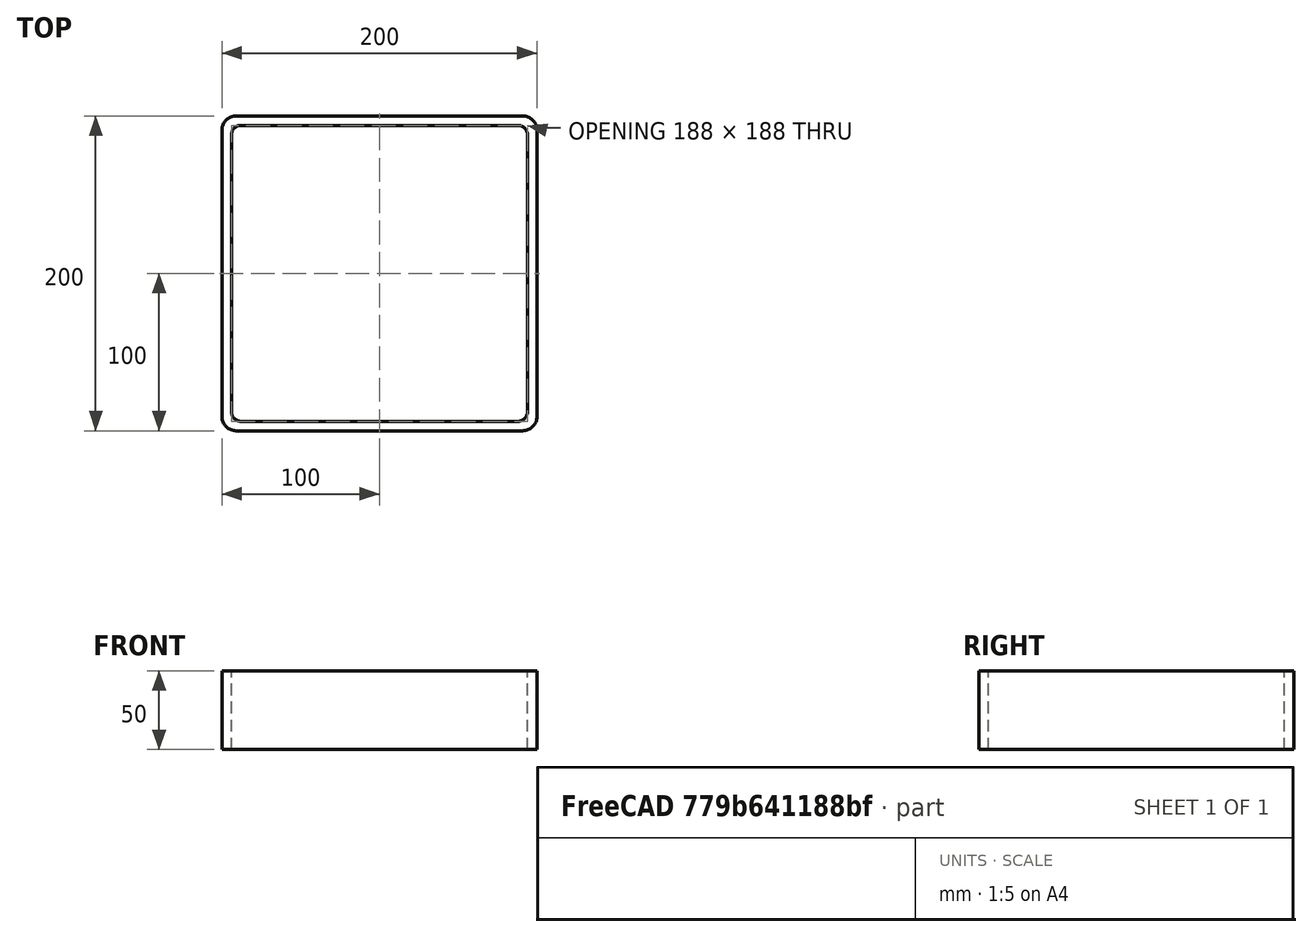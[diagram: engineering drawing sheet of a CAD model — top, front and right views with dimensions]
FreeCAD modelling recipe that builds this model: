
FCSTD DOCUMENT  (FreeCAD 0.15R4671 (Git))
Label: Square hollow section 200x200x6 EN10219 S235JRH
License: All rights reserved
LicenseURL: http://en.wikipedia.org/wiki/All_rights_reserved
objects: Sketcher::SketchObject×1, Part::Extrusion×1
note: 2 computed .brp shape members not serialized (recipe doc carries the construction recipe); baked Part::Feature solids carry a one-line shape summary decoded from their .brp

FEATURE [Sketcher::SketchObject] Sketch
  sketch-geometry (16):
    g0: LineSegment StartX=-88 StartY=94 StartZ=0 EndX=88 EndY=94 EndZ=0
    g1: LineSegment StartX=94 StartY=88 StartZ=0 EndX=94 EndY=-88 EndZ=0
    g2: LineSegment StartX=88 StartY=-94 StartZ=0 EndX=-88 EndY=-94 EndZ=0
    g3: LineSegment StartX=-94 StartY=-88 StartZ=0 EndX=-94 EndY=88 EndZ=0
    g4: LineSegment StartX=-91 StartY=100 StartZ=0 EndX=91 EndY=100 EndZ=0
    g5: LineSegment StartX=100 StartY=91 StartZ=0 EndX=100 EndY=-91 EndZ=0
    g6: LineSegment StartX=91 StartY=-100 StartZ=0 EndX=-91 EndY=-100 EndZ=0
    g7: LineSegment StartX=-100 StartY=-91 StartZ=0 EndX=-100 EndY=91 EndZ=0
    g8: ArcOfCircle CenterX=-88 CenterY=88 CenterZ=0 NormalX=0 NormalY=0 NormalZ=1 Radius=6 StartAngle=1.5708 EndAngle=3.14159
    g9: ArcOfCircle CenterX=88 CenterY=88 CenterZ=0 NormalX=0 NormalY=0 NormalZ=1 Radius=6 StartAngle=0 EndAngle=1.5708
    g10: ArcOfCircle CenterX=88 CenterY=-88 CenterZ=0 NormalX=0 NormalY=0 NormalZ=1 Radius=6 StartAngle=4.71239 EndAngle=6.28319
    g11: ArcOfCircle CenterX=-88 CenterY=-88 CenterZ=0 NormalX=0 NormalY=0 NormalZ=1 Radius=6 StartAngle=3.14159 EndAngle=4.71239
    g12: ArcOfCircle CenterX=91 CenterY=91 CenterZ=0 NormalX=0 NormalY=0 NormalZ=1 Radius=9 StartAngle=0 EndAngle=1.5708
    g13: ArcOfCircle CenterX=91 CenterY=-91 CenterZ=0 NormalX=0 NormalY=0 NormalZ=1 Radius=9 StartAngle=4.71239 EndAngle=6.28319
    g14: ArcOfCircle CenterX=-91 CenterY=-91 CenterZ=0 NormalX=0 NormalY=0 NormalZ=1 Radius=9 StartAngle=3.14159 EndAngle=4.71239
    g15: ArcOfCircle CenterX=-91 CenterY=91 CenterZ=0 NormalX=0 NormalY=0 NormalZ=1 Radius=9 StartAngle=1.5708 EndAngle=3.14159
  constraints (36):
    c: Horizontal(g2)
    c: Vertical(g3)
    c: Horizontal(g6)
    c: Vertical(g7)
    c: Tangent(g3,g8) = 1.5708
    c: Tangent(g0,g8) = 1.5708
    c: Tangent(g0,g9) = 1.5708
    c: Tangent(g1,g9) = 1.5708
    c: Tangent(g1,g10) = 1.5708
    c: Tangent(g2,g10) = 1.5708
    c: Tangent(g2,g11) = 1.5708
    c: Tangent(g3,g11) = 1.5708
    c: Tangent(g4,g12) = 1.5708
    c: Tangent(g5,g12) = 1.5708
    c: Tangent(g5,g13) = 1.5708
    c: Tangent(g6,g13) = 1.5708
    c: Tangent(g6,g14) = 1.5708
    c: Tangent(g7,g14) = 1.5708
    c: Tangent(g7,g15) = 1.5708
    c: Tangent(g4,g15) = 1.5708
    c: Equal(g9,g8)
    c: Equal(g9,g11)
    c: Equal(g9,g10)
    c: Equal(g12,g15)
    c: Equal(g12,g14)
    c: Equal(g12,g13)
    c: Symmetric(g4,g6,g-1)
    c: Symmetric(g7,g5,g-2)
    c: DistanceY(g4,g6) = -200
    c: DistanceX(g7,g5) = 200
    c: Symmetric(g3,g1,g-2)
    c: Symmetric(g0,g2,g-1)
    c: DistanceY(g0,g4) = 6
    c: DistanceX(g5,g1) = -6
    c: Radius(g9) = 6
    c: Radius(g12) = 9
FEATURE [Part::Extrusion] Extrude  label="Square hollow section 200x200x6 EN10219 S235JRH"
  Base = -> Sketch
  Dir = (0,0,50)
  Solid = true
